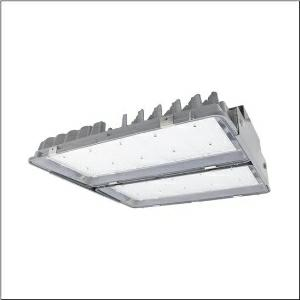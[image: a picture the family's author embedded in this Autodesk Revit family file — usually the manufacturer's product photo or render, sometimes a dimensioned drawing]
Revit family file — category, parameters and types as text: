
# Revit family: highbay_11xtreme_51hf82db4vma
name_source: partatom
category: Lighting Fixtures
units: mm (PartAtom-declared; Revit-internal decimal feet)

## family parameters
Cut with Voids When Loaded = No
Host = Face
Light Source = No
Part Type = Normal
Room Calculation Point = No
Round Connector Dimension = Use Diameter
Shared = No

## types (1)
- --- (1 x LED, 68500 lm, 380.3 W, 4000K)
    Apparent Load = 380 VA
    CIE Flux Codes = 84 96 100 100 100
    Color Rendering = 80
    Color Temperature = 4000K
    Default Elevation = 1800 mm
    Description = Highbay 11Xtreme, high bay luminaire, primary light control with lens, of PMMA, primary optical cover: cover, of toughened safety glass, light emission: direct distribution, primary light characteristic: symmetric, installation type: suspended mounting, surface-mounted, 2x LED module,for 1x 2x LED, rated luminous flux: 68.500lm, luminous efficacy: 180lm/W, light colour: 840, colour temperature: 4000K, control gear: DALI 2 (with two DALI addresses), with cable H07RN-F 5x 1.5mm², mains connection: 220..240V, AC, 50/60Hz, cable length: 1,5m, rated input power: 380W, luminaire housing, of diecast aluminium, partly coated, silver, length: 595mm, width: 560mm, height: 195mm, protection rating (complete): IP66, insulation class (complete): insulation class I (protective earthing), certification: CE, ENEC, UKCA, protection symbol: D, ball protection: ball impact resistant according to DIN VDE 0710 part 13 (with chain suspension), impact resistance: IK08, permissible operating ambient temperature: -25..+45°C, reducing of maximum allowable ambient temperature of 5°C with ceiling mounting, packaging unit: 1 piece
    Height = 157 mm
    Lamp = 1 x LED
    Lamp Light Flux = 68500 lm
    Lamp Power = 380.3 W
    Lamp count = 1
    Length = 593 mm
    Luminous efficacy = 180 lm/W
    Manufacturer = Siteco
    ModVariant = No
    Model = 51HF82DB4VMA
    Mounting Place = Ceiling
    Mounting Type = Pendant
    Number of Poles = 1
    OnlyDefault = Yes
    Power Factor = 1
    Product Name = Highbay 11Xtreme
    Product group = high bay luminaire
    ProductGroupID = 902
    Protection Class = Protection class I
    Protection Degree = IP 66
    RLX_Detail_Level = 1
    RLX_Emergency_Light_Flux = 0 lm
    RLX_Emergency_Type = 0
    RLX_Emergency_Type_DB = No
    RlxData = <blob elided: 34373 chars, md5=2d07abfb>
    Socket = socket
    Standby Power = 0 W
    System Light Flux = 68500 lm
    System Power = 380 W
    Type Comments = factory setting: luminous flux: 100 % | dim-lin: 254 | 1257 mA
    Type Image = l_1258340.jpg
    URL = http://relux.com
    VarID = @adj_088113
    Voltage = 0 V
    Weight = 0.00 kg
    Width = 568 mm

## geometry (parser evidence)
native form markers: Blend x4, Sweep x11
no freeform markers — native parametric forms only
